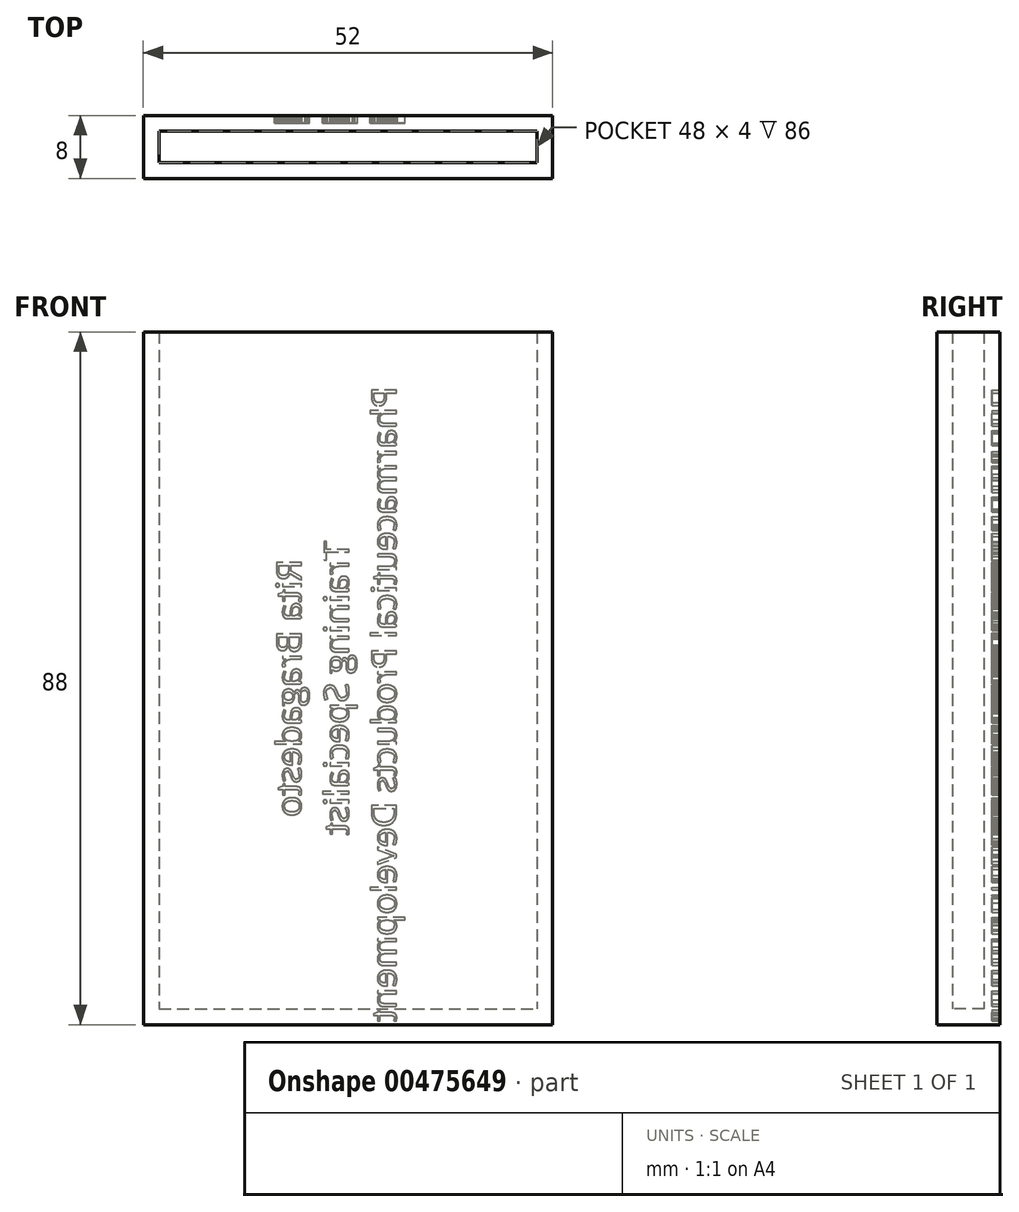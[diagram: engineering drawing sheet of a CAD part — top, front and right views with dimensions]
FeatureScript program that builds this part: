
annotation { "Feature Type Name" : "Feature", "Feature Type Description" : "" }
export const myFeature = defineFeature(function(context is Context, id is Id, definition is map)
    precondition{}
    {
        {
            var Q0;
            Q0=qCreatedBy(makeId("Top.planeOp"),FACE);
            var sketch = newSketch(context, id + "F0", { "sketchPlane" : qUnion([Q0])});
            skLineSegment(sketch, "E0.bottom", {"start": v(-23.06, 3.94) * mm, "end": v(28.94, 3.94) * mm});
            skLineSegment(sketch, "E0.top", {"start": v(-23.06, -4.06) * mm, "end": v(28.94, -4.06) * mm});
            skLineSegment(sketch, "E0.left", {"start": v(-23.06, 3.94) * mm, "end": v(-23.06, -4.06) * mm});
            skLineSegment(sketch, "E0.right", {"start": v(28.94, 3.94) * mm, "end": v(28.94, -4.06) * mm});
            skLineSegment(sketch, "E1.0", {"start": v(-21.06, -2.06) * mm, "end": v(26.94, -2.06) * mm});
            skLineSegment(sketch, "E1.1", {"start": v(-21.06, 1.94) * mm, "end": v(-21.06, -2.06) * mm});
            skLineSegment(sketch, "E1.2", {"start": v(-21.06, 1.94) * mm, "end": v(26.94, 1.94) * mm});
            skLineSegment(sketch, "E1.3", {"start": v(26.94, 1.94) * mm, "end": v(26.94, -2.06) * mm});
            skSolve(sketch);
        }
        {
            var Q0;
            Q0=makeQuery(id+"F0.imprint","IMPRINT",FACE,{"disambiguationData":[TD([[makeQuery(id+"F0.imprint","IMPRINT",EDGE,{"derivedFrom":sQuery(id+"F0.wireOp",EDGE,"E0.bottom")}),-1.0]])]});
            extrude(context, id + "F1", {"entities" : qUnion([Q0]), "depth" : 88 * mm});
        }
        {
            var Q0;
            Q0=makeQuery(id+"F1.opExtrude","CAP_FACE",FACE,{"disambiguationData":[OSD([sQuery(id+"F0.wireOp",EDGE,"E0.bottom"),sQuery(id+"F0.wireOp",EDGE,"E0.top"),sQuery(id+"F0.wireOp",EDGE,"E0.left"),sQuery(id+"F0.wireOp",EDGE,"E0.right"),sQuery(id+"F0.wireOp",EDGE,"E1.0"),sQuery(id+"F0.wireOp",EDGE,"E1.1"),sQuery(id+"F0.wireOp",EDGE,"E1.2"),sQuery(id+"F0.wireOp",EDGE,"E1.3")])],"isStart":true});
            var sketch = newSketch(context, id + "F2", { "sketchPlane" : qUnion([Q0])});
            skLineSegment(sketch, "E2.bottom", {"start": v(-21.06, 2.06) * mm, "end": v(26.94, 2.06) * mm});
            skLineSegment(sketch, "E2.top", {"start": v(-21.06, -1.94) * mm, "end": v(26.94, -1.94) * mm});
            skLineSegment(sketch, "E2.left", {"start": v(-21.06, 2.06) * mm, "end": v(-21.06, -1.94) * mm});
            skLineSegment(sketch, "E2.right", {"start": v(26.94, 2.06) * mm, "end": v(26.94, -1.94) * mm});
            skSolve(sketch);
        }
        {
            var Q0;
            Q0=makeQuery(id+"F2.imprint","IMPRINT",FACE,{"disambiguationData":[TD([[makeQuery(id+"F2.imprint","IMPRINT",EDGE,{"derivedFrom":sQuery(id+"F2.wireOp",EDGE,"E2.bottom")}),-1.0]])]});
            extrude(context, id + "F3", {"entities" : qUnion([Q0]), "operationType" : NewBodyOperationType.ADD, "oppositeDirection" : true, "depth" : 2 * mm});
        }
        {
            var Q0;
            Q0=makeQuery(id+"F1.opExtrude","SWEPT_FACE",FACE,{"disambiguationData":[OSD([sQuery(id+"F0.wireOp",EDGE,"E0.bottom")])]});
            var sketch = newSketch(context, id + "F4", { "sketchPlane" : qUnion([Q0])});
            skText(sketch, "E3", { "text": "                         Rita Bragadesto\n                       Training Specialist \n      Pharmaceutical Products Development       ", "fontName": "OpenSans-Regular.ttf"});
            const initialGuessF4  = {"E3": [0.00299, 0.088, 0, -1, 0.0032]};
            skSetInitialGuess(sketch, initialGuessF4);
            skSolve(sketch);
        }
        {
            var Q0;
            Q0 = qSketchRegion(id + "F4", true);
            extrude(context, id + "F5", {"entities" : qUnion([Q0]), "operationType" : NewBodyOperationType.REMOVE, "oppositeDirection" : true, "depth" : 1 * mm});
        }
    });
